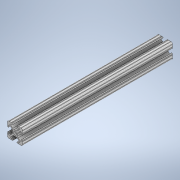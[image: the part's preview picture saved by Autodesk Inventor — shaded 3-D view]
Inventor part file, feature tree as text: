
AUTODESK INVENTOR PART (.ipt)
format: ipt  version: 2020 (Build 240168000, 168)  size: 235,008 bytes
history: native  units: in
note: dims shown in document units (in); Inventor stores cm internally (conversion verified against a paired STEP export)
features: extrude x1, sketch x1
ambient origin geometry x8: Origin, YZ Plane, XZ Plane, XY Plane, X Axis, Y Axis, Z Axis, Center Point
bodies: Solid1 (feature_tree)
feature tree (2):
  extrude  "Extrusion1"  [1 undecoded]
  sketch  "Sketch1"  dims[d0=10.0in d1=0.0in]
note: 1 required parameter value undecoded (feature->parameter linkage not recoverable at this tier; creation-order binding heuristic only, values carry confidence <= 0.55)
